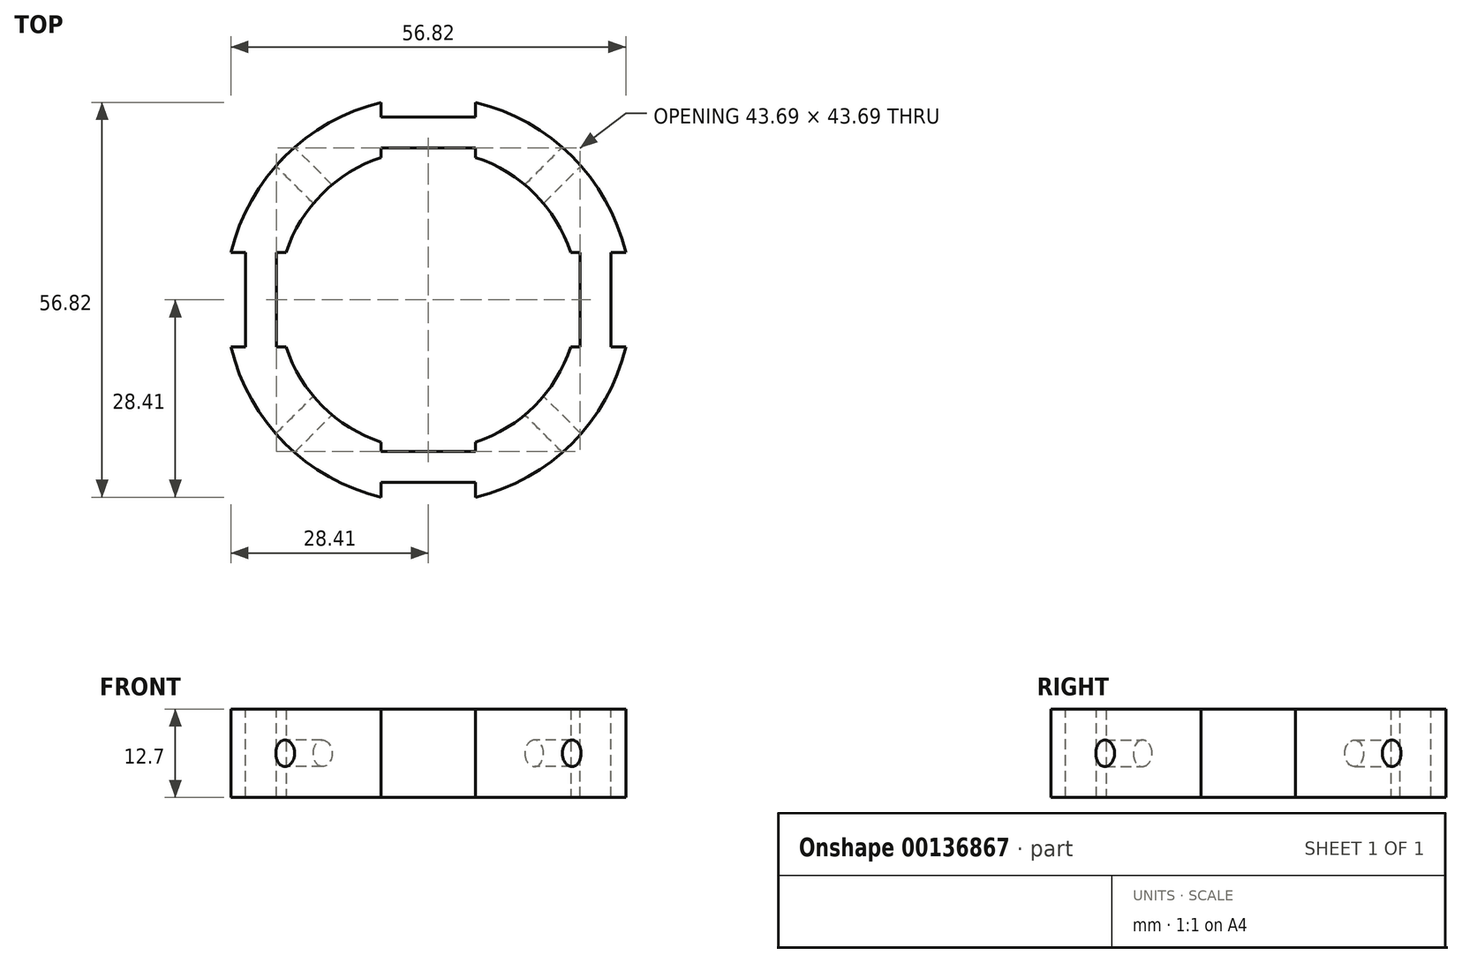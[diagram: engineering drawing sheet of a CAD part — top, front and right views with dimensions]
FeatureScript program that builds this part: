
annotation { "Feature Type Name" : "Feature", "Feature Type Description" : "" }
export const myFeature = defineFeature(function(context is Context, id is Id, definition is map)
    precondition{}
    {
        {
            var Q0;
            Q0=qCreatedBy(makeId("Top.planeOp"),FACE);
            var sketch = newSketch(context, id + "F0", { "sketchPlane" : qUnion([Q0])});
            skCircle(sketch, "E0", {"center": v(0, 0) * mm, "radius": 21.59 * mm});
            skCircle(sketch, "E1", {"center": v(0, 0) * mm, "radius": 29.21 * mm});
            skSolve(sketch);
        }
        {
            var Q0;
            Q0=makeQuery(id+"F0.imprint","IMPRINT",FACE,{"disambiguationData":[TD([[makeQuery(id+"F0.imprint","IMPRINT",EDGE,{"derivedFrom":sQuery(id+"F0.wireOp",EDGE,"E0")}),-1.0]])]});
            extrude(context, id + "F1", {"entities" : qUnion([Q0]), "depth" : 12.7 * mm});
        }
        {
            var Q0;
            Q0=makeQuery(id+"F1.opExtrude","CAP_FACE",FACE,{"disambiguationData":[OSD([sQuery(id+"F0.wireOp",EDGE,"E0"),sQuery(id+"F0.wireOp",EDGE,"E1")])],"isStart":false});
            var sketch = newSketch(context, id + "F2", { "sketchPlane" : qUnion([Q0])});
            skLineSegment(sketch, "E2.bottom", {"start": v(6.8, 18.29) * mm, "end": v(-6.8, 18.29) * mm});
            skLineSegment(sketch, "E2.top", {"start": v(6.8, 21.84) * mm, "end": v(-6.8, 21.84) * mm});
            skLineSegment(sketch, "E2.left", {"start": v(6.8, 18.29) * mm, "end": v(6.8, 21.84) * mm});
            skLineSegment(sketch, "E2.right", {"start": v(-6.8, 18.29) * mm, "end": v(-6.8, 21.84) * mm});
            skPoint(sketch, "E2.middle", {"position": v(0, 20.07) * mm});
            skLineSegment(sketch, "E3.bottom", {"start": v(6.8, 26.29) * mm, "end": v(-6.8, 26.29) * mm});
            skLineSegment(sketch, "E3.top", {"start": v(6.8, 29.85) * mm, "end": v(-6.8, 29.85) * mm});
            skLineSegment(sketch, "E3.left", {"start": v(6.8, 26.29) * mm, "end": v(6.8, 29.85) * mm});
            skLineSegment(sketch, "E3.right", {"start": v(-6.8, 26.29) * mm, "end": v(-6.8, 29.85) * mm});
            skPoint(sketch, "E3.middle", {"position": v(0, 28.07) * mm});
            skPoint(sketch, "E4.1.0", {"position": v(-20.07, 0) * mm});
            skLineSegment(sketch, "E4.1.1", {"start": v(-18.29, 6.8) * mm, "end": v(-21.84, 6.8) * mm});
            skLineSegment(sketch, "E4.1.2", {"start": v(-26.29, 6.8) * mm, "end": v(-29.85, 6.8) * mm});
            skLineSegment(sketch, "E4.1.3", {"start": v(-26.29, 6.8) * mm, "end": v(-26.29, -6.8) * mm});
            skLineSegment(sketch, "E4.1.4", {"start": v(-18.29, -6.8) * mm, "end": v(-21.84, -6.8) * mm});
            skLineSegment(sketch, "E4.1.5", {"start": v(-21.84, 6.8) * mm, "end": v(-21.84, -6.8) * mm});
            skLineSegment(sketch, "E4.1.6", {"start": v(-29.85, 6.8) * mm, "end": v(-29.84, -6.8) * mm});
            skLineSegment(sketch, "E4.1.7", {"start": v(-26.29, -6.8) * mm, "end": v(-29.85, -6.8) * mm});
            skPoint(sketch, "E4.1.8", {"position": v(-28.07, 0) * mm});
            skLineSegment(sketch, "E4.1.9", {"start": v(-18.29, 6.8) * mm, "end": v(-18.29, -6.8) * mm});
            skPoint(sketch, "E4.2.0", {"position": v(0, -20.07) * mm});
            skLineSegment(sketch, "E4.2.1", {"start": v(-6.8, -18.29) * mm, "end": v(-6.8, -21.84) * mm});
            skLineSegment(sketch, "E4.2.2", {"start": v(-6.8, -26.29) * mm, "end": v(-6.8, -29.85) * mm});
            skLineSegment(sketch, "E4.2.3", {"start": v(-6.8, -26.29) * mm, "end": v(6.8, -26.29) * mm});
            skLineSegment(sketch, "E4.2.4", {"start": v(6.8, -18.29) * mm, "end": v(6.8, -21.84) * mm});
            skLineSegment(sketch, "E4.2.5", {"start": v(-6.8, -21.84) * mm, "end": v(6.8, -21.84) * mm});
            skLineSegment(sketch, "E4.2.6", {"start": v(-6.8, -29.85) * mm, "end": v(6.8, -29.85) * mm});
            skLineSegment(sketch, "E4.2.7", {"start": v(6.8, -26.29) * mm, "end": v(6.8, -29.85) * mm});
            skPoint(sketch, "E4.2.8", {"position": v(0, -28.07) * mm});
            skLineSegment(sketch, "E4.2.9", {"start": v(-6.8, -18.29) * mm, "end": v(6.8, -18.29) * mm});
            skPoint(sketch, "E4.3.0", {"position": v(20.07, 0) * mm});
            skLineSegment(sketch, "E4.3.1", {"start": v(18.29, -6.8) * mm, "end": v(21.84, -6.8) * mm});
            skLineSegment(sketch, "E4.3.2", {"start": v(26.29, -6.8) * mm, "end": v(29.85, -6.8) * mm});
            skLineSegment(sketch, "E4.3.3", {"start": v(26.29, -6.8) * mm, "end": v(26.29, 6.8) * mm});
            skLineSegment(sketch, "E4.3.4", {"start": v(18.29, 6.8) * mm, "end": v(21.84, 6.8) * mm});
            skLineSegment(sketch, "E4.3.5", {"start": v(21.84, -6.8) * mm, "end": v(21.84, 6.8) * mm});
            skLineSegment(sketch, "E4.3.6", {"start": v(29.85, -6.8) * mm, "end": v(29.85, 6.8) * mm});
            skLineSegment(sketch, "E4.3.7", {"start": v(26.29, 6.8) * mm, "end": v(29.85, 6.8) * mm});
            skPoint(sketch, "E4.3.8", {"position": v(28.07, 0) * mm});
            skLineSegment(sketch, "E4.3.9", {"start": v(18.29, -6.8) * mm, "end": v(18.29, 6.8) * mm});
            skPoint(sketch, "E4.center", {"position": v(0, 0) * mm});
            skSolve(sketch);
        }
        {
            var Q0;
            Q0 = qSketchRegion(id + "F2", true);
            extrude(context, id + "F3", {"entities" : qUnion([Q0]), "operationType" : NewBodyOperationType.REMOVE, "oppositeDirection" : true, "depth" : 25.4 * mm});
        }
        {
            var Q0;
            {var subQ0=sQuery(id+"F0.wireOp",EDGE,"E0");Q0=makeQuery(id+"F3.boolean.opBoolean","SPLIT",EDGE,{"disambiguationData":[TD([makeQuery(id+"F3.opExtrude","SWEPT_FACE",FACE,{"disambiguationData":[OSD([sQuery(id+"F2.wireOp",EDGE,"E4.1.4")])]})])],"derivedFrom":makeQuery(id+"F1.opExtrude","CAP_EDGE",EDGE,{"disambiguationData":[OSD([subQ0])],"isStart":false})});}
            cPoint(context, id + "F4", {"entities" : qUnion([Q0]), "parameter" : 0.5});
        }
        {
            var Q0;
            {var subQ0=sQuery(id+"F0.wireOp",EDGE,"E0");Q0=makeQuery(id+"F3.boolean.opBoolean","SPLIT",EDGE,{"disambiguationData":[TD([makeQuery(id+"F3.opExtrude","SWEPT_FACE",FACE,{"disambiguationData":[OSD([sQuery(id+"F2.wireOp",EDGE,"E2.left")])]})])],"derivedFrom":makeQuery(id+"F1.opExtrude","CAP_EDGE",EDGE,{"disambiguationData":[OSD([subQ0])],"isStart":false})});}
            cPoint(context, id + "F5", {"entities" : qUnion([Q0]), "parameter" : 0.5});
        }
        {
            var Q0;
            Q0=qCreatedBy(makeId("Origin.pointOp"),VERTEX);
            var Q1;
            Q1 = qCreatedBy(id + "F4" ,VERTEX);
            var Q2;
            Q2 = qCreatedBy(id + "F5" ,VERTEX);
            cPlane(context, id + "F6", {"entities" : qUnion([Q0, Q1, Q2]), "cplaneType" : CPlaneType.THREE_POINT, "offset" : 25.4 * mm, "width" : 152.4 * mm, "height" : 152.4 * mm});
        }
        {
            var Q0;
            Q0=qCreatedBy(id+"F6.planeOp",FACE);
            var sketch = newSketch(context, id + "F7", { "sketchPlane" : qUnion([Q0])});
            skCircle(sketch, "E5", {"center": v(0, 6.35) * mm, "radius": 1.9 * mm});
            skSolve(sketch);
        }
        {
            var Q0;
            Q0 = qSketchRegion(id + "F7", true);
            extrude(context, id + "F8", {"entities" : qUnion([Q0]), "operationType" : NewBodyOperationType.REMOVE, "endBound" : BoundingType.SYMMETRIC, "depth" : 787.4 * mm});
        }
        {
            var Q0;
            {var subQ0=sQuery(id+"F0.wireOp",EDGE,"E0");Q0=makeQuery(id+"F3.boolean.opBoolean","SPLIT",EDGE,{"disambiguationData":[TD([makeQuery(id+"F3.opExtrude","SWEPT_FACE",FACE,{"disambiguationData":[OSD([sQuery(id+"F2.wireOp",EDGE,"E4.2.4")])]})])],"derivedFrom":makeQuery(id+"F1.opExtrude","CAP_EDGE",EDGE,{"disambiguationData":[OSD([subQ0])],"isStart":false})});}
            cPoint(context, id + "F9", {"entities" : qUnion([Q0]), "parameter" : 0.5});
        }
        {
            var Q0;
            {var subQ0=sQuery(id+"F0.wireOp",EDGE,"E0");Q0=makeQuery(id+"F3.boolean.opBoolean","SPLIT",EDGE,{"disambiguationData":[TD([makeQuery(id+"F3.opExtrude","SWEPT_FACE",FACE,{"disambiguationData":[OSD([sQuery(id+"F2.wireOp",EDGE,"E2.right")])]})])],"derivedFrom":makeQuery(id+"F1.opExtrude","CAP_EDGE",EDGE,{"disambiguationData":[OSD([subQ0])],"isStart":false})});}
            cPoint(context, id + "F10", {"entities" : qUnion([Q0]), "parameter" : 0.5});
        }
        {
            var Q0;
            Q0 = qCreatedBy(id + "F9" ,VERTEX);
            var Q1;
            Q1 = qCreatedBy(id + "F10" ,VERTEX);
            var Q2;
            Q2=qCreatedBy(makeId("Origin.pointOp"),VERTEX);
            cPlane(context, id + "F11", {"entities" : qUnion([Q0, Q1, Q2]), "cplaneType" : CPlaneType.THREE_POINT, "offset" : 25.4 * mm, "width" : 152.4 * mm, "height" : 152.4 * mm});
        }
        {
            var Q0;
            Q0=qCreatedBy(id+"F11.planeOp",FACE);
            var sketch = newSketch(context, id + "F12", { "sketchPlane" : qUnion([Q0])});
            skCircle(sketch, "E6", {"center": v(0, 6.35) * mm, "radius": 1.9 * mm});
            skSolve(sketch);
        }
        {
            var Q0;
            Q0 = qSketchRegion(id + "F12", true);
            extrude(context, id + "F13", {"entities" : qUnion([Q0]), "operationType" : NewBodyOperationType.REMOVE, "endBound" : BoundingType.SYMMETRIC, "oppositeDirection" : true, "depth" : 76.2 * mm});
        }
    });
